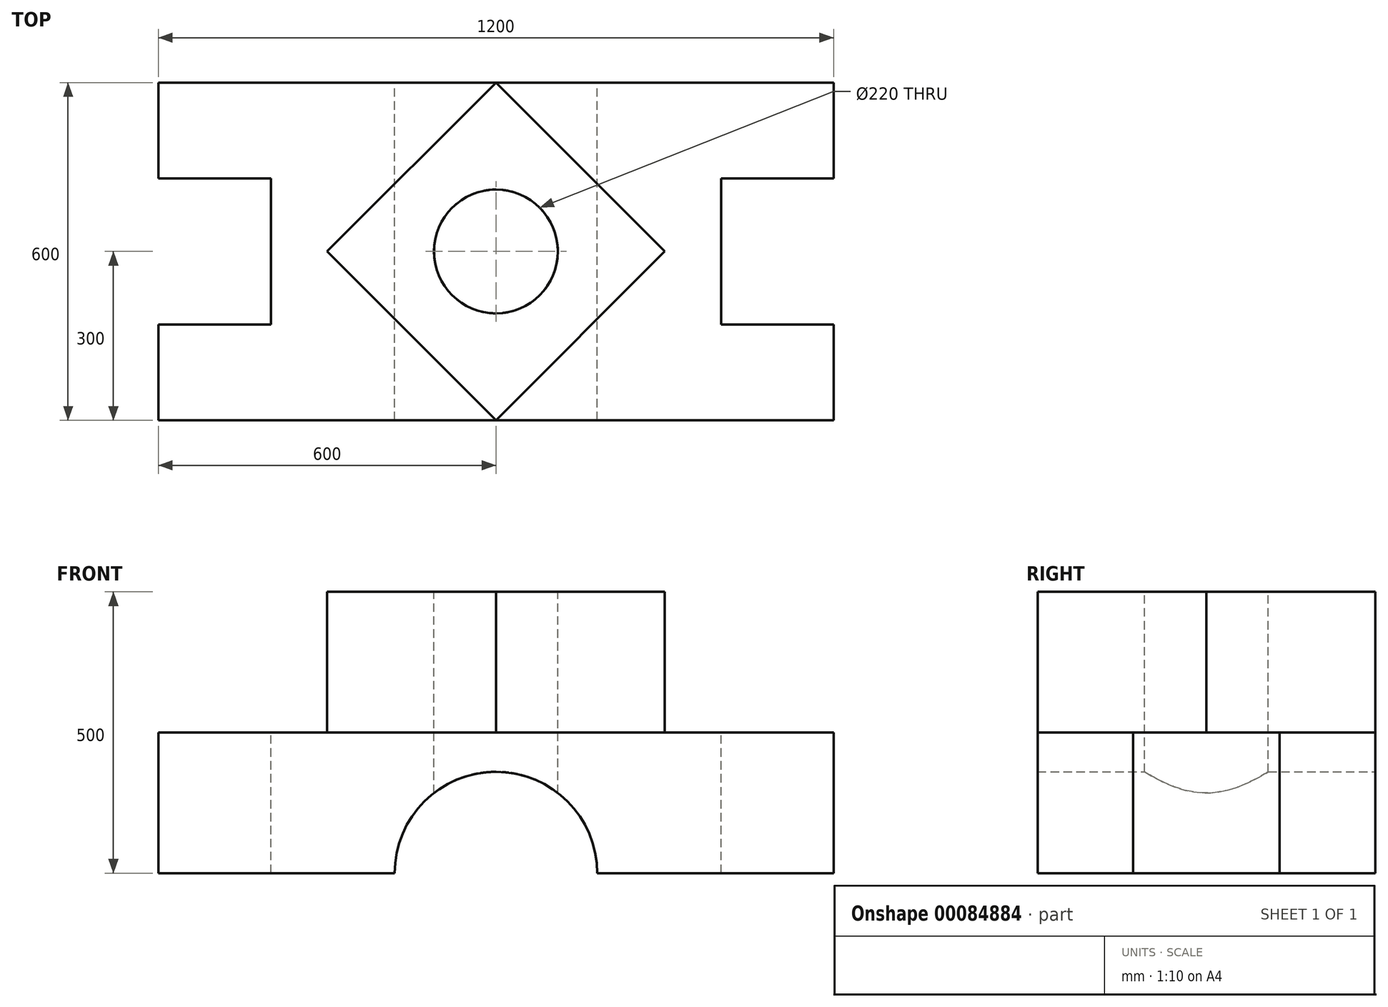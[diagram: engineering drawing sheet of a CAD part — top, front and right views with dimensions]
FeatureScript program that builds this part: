
annotation { "Feature Type Name" : "Feature", "Feature Type Description" : "" }
export const myFeature = defineFeature(function(context is Context, id is Id, definition is map)
    precondition{}
    {
        {
            var Q0;
            Q0=qCreatedBy(makeId("Front.planeOp"),FACE);
            var sketch = newSketch(context, id + "F0", { "sketchPlane" : qUnion([Q0])});
            skLineSegment(sketch, "E0.top", {"start": v(-300, 250) * mm, "end": v(300, 250) * mm});
            skLineSegment(sketch, "E0.left", {"start": v(-600, -250) * mm, "end": v(-600, 0) * mm});
            skLineSegment(sketch, "E0.right", {"start": v(600, -250) * mm, "end": v(600, 0) * mm});
            skPoint(sketch, "E0.middle", {"position": v(0, 0) * mm});
            skLineSegment(sketch, "E1", {"start": v(-300, 250) * mm, "end": v(-300, 0) * mm});
            skLineSegment(sketch, "E2", {"start": v(-300, 0) * mm, "end": v(-600, 0) * mm});
            skLineSegment(sketch, "E3", {"start": v(300, 250) * mm, "end": v(300, 0) * mm});
            skLineSegment(sketch, "E4", {"start": v(300, 0) * mm, "end": v(600, 0) * mm});
            skPoint(sketch, "E5.orphan", {"position": v(-600, 250) * mm});
            skPoint(sketch, "E6.orphan", {"position": v(600, 250) * mm});
            skLineSegment(sketch, "E7", {"start": v(-600, -250) * mm, "end": v(-180, -250) * mm});
            skArc(sketch, "E8", {"start": v(180, -250) * mm, "mid": v(0, -70) * mm, "end": v(-180, -250) * mm});
            skLineSegment(sketch, "E9.trimOffspring", {"start": v(180, -250) * mm, "end": v(600, -250) * mm});
            skSolve(sketch);
        }
        {
            var Q0;
            Q0 = qSketchRegion(id + "F0", true);
            extrude(context, id + "F1", {"entities" : qUnion([Q0]), "depth" : 600 * mm, "offsetDistance" : 25 * mm});
        }
        {
            var Q0;
            Q0=makeQuery(id+"F1.opExtrude","SWEPT_FACE",FACE,{"disambiguationData":[OSD([sQuery(id+"F0.wireOp",EDGE,"E4")])]});
            var sketch = newSketch(context, id + "F2", { "sketchPlane" : qUnion([Q0])});
            skLineSegment(sketch, "E10.bottom", {"start": v(800, -430) * mm, "end": v(400, -430) * mm});
            skLineSegment(sketch, "E10.top", {"start": v(800, -170) * mm, "end": v(400, -170) * mm});
            skLineSegment(sketch, "E10.left", {"start": v(800, -430) * mm, "end": v(800, -170) * mm});
            skLineSegment(sketch, "E10.right", {"start": v(400, -430) * mm, "end": v(400, -170) * mm});
            skPoint(sketch, "E10.middle", {"position": v(600, -300) * mm});
            skSolve(sketch);
        }
        {
            var Q0;
            Q0 = qSketchRegion(id + "F2", true);
            extrude(context, id + "F3", {"entities" : qUnion([Q0]), "operationType" : NewBodyOperationType.REMOVE, "endBound" : BoundingType.THROUGH_ALL, "depth" : 25 * mm});
        }
        {
            var Q0;
            Q0 = qSketchRegion(id + "F2", true);
            extrude(context, id + "F4", {"entities" : qUnion([Q0]), "operationType" : NewBodyOperationType.REMOVE, "endBound" : BoundingType.THROUGH_ALL, "oppositeDirection" : true, "depth" : 25 * mm});
        }
        {
            var Q0;
            Q0=makeQuery(id+"F1.opExtrude","SWEPT_FACE",FACE,{"disambiguationData":[OSD([sQuery(id+"F0.wireOp",EDGE,"E2")])]});
            var sketch = newSketch(context, id + "F5", { "sketchPlane" : qUnion([Q0])});
            skLineSegment(sketch, "E11.bottom", {"start": v(-800, -430) * mm, "end": v(-400, -430) * mm});
            skLineSegment(sketch, "E11.top", {"start": v(-800, -170) * mm, "end": v(-400, -170) * mm});
            skLineSegment(sketch, "E11.left", {"start": v(-800, -430) * mm, "end": v(-800, -170) * mm});
            skLineSegment(sketch, "E11.right", {"start": v(-400, -430) * mm, "end": v(-400, -170) * mm});
            skPoint(sketch, "E11.middle", {"position": v(-600, -300) * mm});
            skSolve(sketch);
        }
        {
            var Q0;
            Q0 = qSketchRegion(id + "F5", true);
            extrude(context, id + "F6", {"entities" : qUnion([Q0]), "operationType" : NewBodyOperationType.REMOVE, "endBound" : BoundingType.THROUGH_ALL, "oppositeDirection" : true, "depth" : 25 * mm, "offsetDistance" : 25 * mm});
        }
        {
            var Q0;
            Q0=makeQuery(id+"F1.opExtrude","SWEPT_FACE",FACE,{"disambiguationData":[OSD([sQuery(id+"F0.wireOp",EDGE,"E0.top")])]});
            var sketch = newSketch(context, id + "F7", { "sketchPlane" : qUnion([Q0])});
            skLineSegment(sketch, "E12", {"start": v(0, 0) * mm, "end": v(-300, -300) * mm});
            skLineSegment(sketch, "E13", {"start": v(-300, -300) * mm, "end": v(-300, 0) * mm});
            skLineSegment(sketch, "E14", {"start": v(-300, 0) * mm, "end": v(0, 0) * mm});
            skLineSegment(sketch, "E15", {"start": v(-300, -300) * mm, "end": v(0, -600) * mm});
            skLineSegment(sketch, "E16", {"start": v(0, -600) * mm, "end": v(-300, -600) * mm});
            skLineSegment(sketch, "E17", {"start": v(-300, -600) * mm, "end": v(-300, -300) * mm});
            skLineSegment(sketch, "E18", {"start": v(0, -600) * mm, "end": v(300, -300) * mm});
            skLineSegment(sketch, "E19", {"start": v(300, -300) * mm, "end": v(300, -600) * mm});
            skLineSegment(sketch, "E20", {"start": v(300, -600) * mm, "end": v(0, -600) * mm});
            skSolve(sketch);
        }
        {
            var Q0;
            Q0 = qSketchRegion(id + "F7", true);
            extrude(context, id + "F8", {"entities" : qUnion([Q0]), "operationType" : NewBodyOperationType.REMOVE, "oppositeDirection" : true, "depth" : 250 * mm, "offsetDistance" : 25 * mm});
        }
        {
            var Q0;
            Q0=makeQuery(id+"F1.opExtrude","SWEPT_FACE",FACE,{"disambiguationData":[OSD([sQuery(id+"F0.wireOp",EDGE,"E0.top")])]});
            var sketch = newSketch(context, id + "F9", { "sketchPlane" : qUnion([Q0])});
            skLineSegment(sketch, "E21", {"start": v(0, 0) * mm, "end": v(300, -300) * mm});
            skLineSegment(sketch, "E22", {"start": v(300, -300) * mm, "end": v(300, 0) * mm});
            skLineSegment(sketch, "E23", {"start": v(300, 0) * mm, "end": v(0, 0) * mm});
            skSolve(sketch);
        }
        {
            var Q0;
            Q0 = qSketchRegion(id + "F9", true);
            extrude(context, id + "F10", {"entities" : qUnion([Q0]), "operationType" : NewBodyOperationType.REMOVE, "oppositeDirection" : true, "depth" : 250 * mm});
        }
        {
            var Q0;
            Q0=makeQuery(id+"F1.opExtrude","SWEPT_FACE",FACE,{"disambiguationData":[OSD([sQuery(id+"F0.wireOp",EDGE,"E0.top")])]});
            var sketch = newSketch(context, id + "F11", { "sketchPlane" : qUnion([Q0])});
            skCircle(sketch, "E24", {"center": v(0, -300) * mm, "radius": 110 * mm});
            skSolve(sketch);
        }
        {
            var Q0;
            Q0 = qSketchRegion(id + "F11", true);
            extrude(context, id + "F12", {"entities" : qUnion([Q0]), "operationType" : NewBodyOperationType.REMOVE, "endBound" : BoundingType.THROUGH_ALL, "oppositeDirection" : true, "depth" : 25 * mm});
        }
    });
